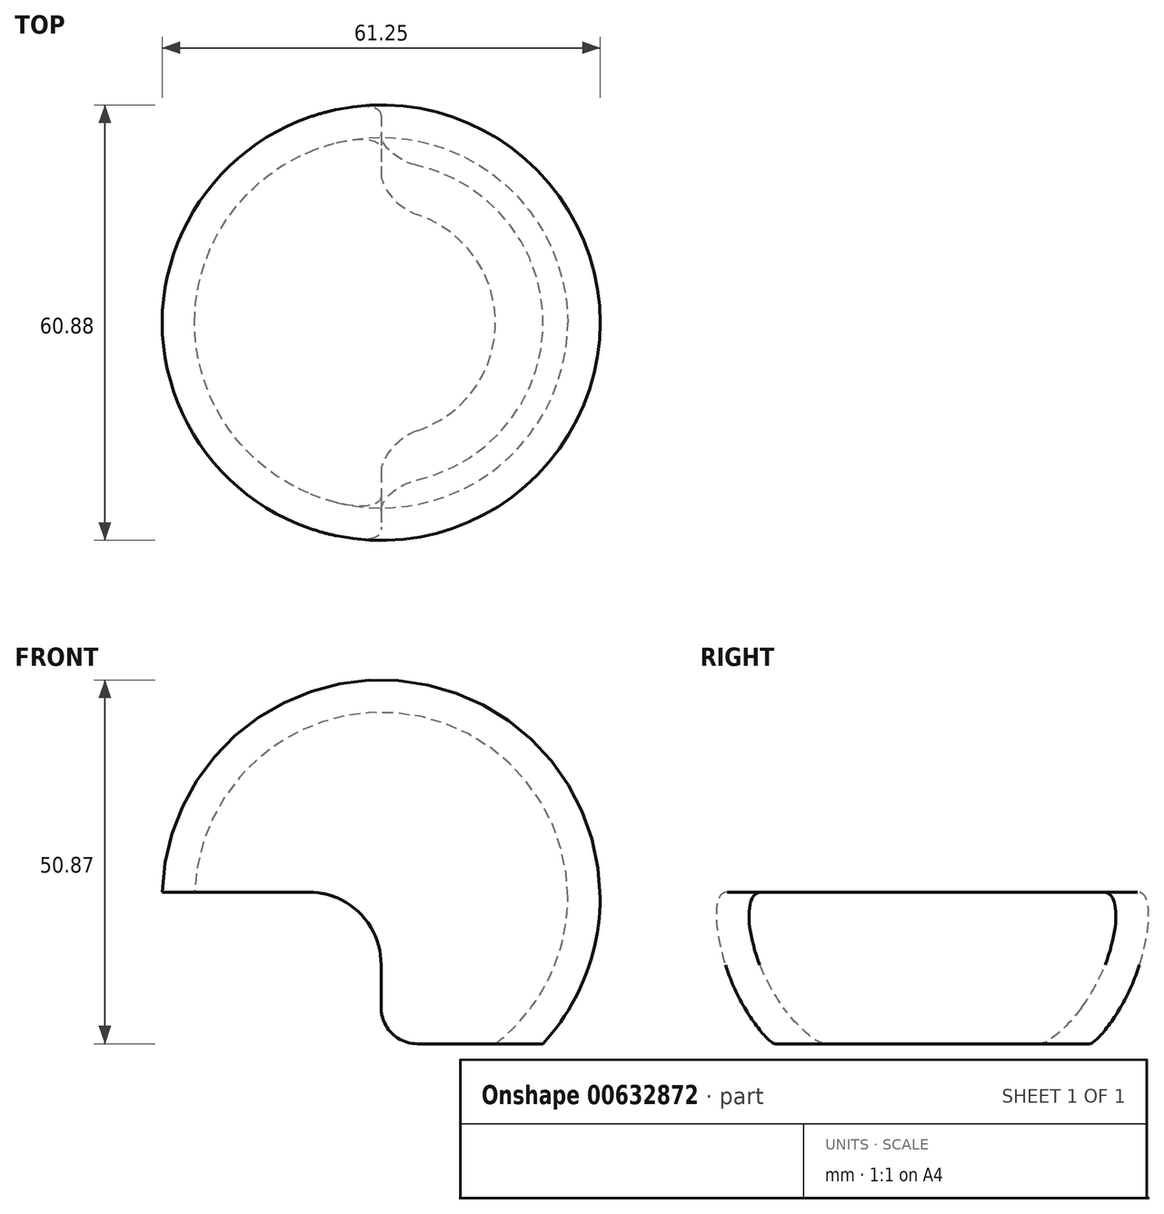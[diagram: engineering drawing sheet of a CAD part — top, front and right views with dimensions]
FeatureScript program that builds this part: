
annotation { "Feature Type Name" : "Feature", "Feature Type Description" : "" }
export const myFeature = defineFeature(function(context is Context, id is Id, definition is map)
    precondition{}
    {
        {
            var Q0;
            Q0=qCreatedBy(makeId("Front.planeOp"),FACE);
            var sketch = newSketch(context, id + "F0", { "sketchPlane" : qUnion([Q0])});
            skArc(sketch, "E0", {"start": v(30.63, 0.2) * mm, "mid": v(0, 30.63) * mm, "end": v(-30.63, 0.2) * mm});
            skLineSegment(sketch, "E1", {"start": v(30.63, 0.2) * mm, "end": v(26.1, 0.2) * mm});
            skArc(sketch, "E2", {"start": v(26.1, 0.2) * mm, "mid": v(0, 26.1) * mm, "end": v(-26.1, 0.2) * mm});
            skLineSegment(sketch, "E3.trimOffspring", {"start": v(-26.1, 0.2) * mm, "end": v(-30.63, 0.2) * mm});
            skSolve(sketch);
        }
        {
            var Q0;
            Q0 = qSketchRegion(id + "F0", true);
            var Q1;
            Q1=sQuery(id+"F0.wireOp",EDGE,"E1");
            revolve(context, id + "F1", {"entities" : qUnion([Q0]), "axis" : qUnion([Q1]), "revolveType" : RevolveType.FULL});
        }
        {
            var Q0;
            Q0=qCreatedBy(makeId("Front.planeOp"),FACE);
            var sketch = newSketch(context, id + "F2", { "sketchPlane" : qUnion([Q0])});
            skLineSegment(sketch, "E4.bottom", {"start": v(0, 0.97) * mm, "end": v(-34.52, 0.97) * mm});
            skLineSegment(sketch, "E4.top", {"start": v(0, -36.46) * mm, "end": v(-34.52, -36.46) * mm});
            skLineSegment(sketch, "E4.left", {"start": v(0, 0.97) * mm, "end": v(0, -36.46) * mm});
            skLineSegment(sketch, "E4.right", {"start": v(-34.52, 0.97) * mm, "end": v(-34.52, -36.46) * mm});
            skLineSegment(sketch, "E5.bottom", {"start": v(0, -36.46) * mm, "end": v(31.12, -36.46) * mm});
            skLineSegment(sketch, "E5.top", {"start": v(0, -20.24) * mm, "end": v(31.12, -20.24) * mm});
            skLineSegment(sketch, "E5.right", {"start": v(31.12, -36.46) * mm, "end": v(31.12, -20.24) * mm});
            skSolve(sketch);
        }
        {
            var Q0;
            Q0 = qSketchRegion(id + "F2", true);
            extrude(context, id + "F3", {"entities" : qUnion([Q0]), "operationType" : NewBodyOperationType.REMOVE, "endBound" : BoundingType.SYMMETRIC, "oppositeDirection" : true, "depth" : 137.16 * mm, "offsetDistance" : 25.4 * mm});
        }
        {
            var Q0;
            Q0=makeQuery(id+"F3.boolean.opBoolean","COPY",EDGE,{"disambiguationData":[OD(1.0)],"derivedFrom":makeQuery(id+"F3.opExtrude","SWEPT_EDGE",EDGE,{"disambiguationData":[OSD([sQuery(id+"F2.wireOp",EDGE,"E4.left"),sQuery(id+"F2.wireOp",EDGE,"E5.top")])]})});
            var Q1;
            Q1=makeQuery(id+"F3.boolean.opBoolean","COPY",EDGE,{"disambiguationData":[OD(0.0)],"derivedFrom":makeQuery(id+"F3.opExtrude","SWEPT_EDGE",EDGE,{"disambiguationData":[OSD([sQuery(id+"F2.wireOp",EDGE,"E4.left"),sQuery(id+"F2.wireOp",EDGE,"E5.top")])]})});
            fillet(context, id + "F4", {"entities" : qUnion([Q0, Q1]), "radius" : 5.08 * mm, "tangentPropagation" : true, "allowEdgeOverflow" : false});
        }
        {
            var Q0;
            Q0=makeQuery(id+"F3.boolean.opBoolean","COPY",EDGE,{"disambiguationData":[OD(1.0)],"derivedFrom":makeQuery(id+"F3.opExtrude","SWEPT_EDGE",EDGE,{"disambiguationData":[OSD([sQuery(id+"F2.wireOp",EDGE,"E4.bottom"),sQuery(id+"F2.wireOp",EDGE,"E4.left")])]})});
            var Q1;
            Q1=makeQuery(id+"F3.boolean.opBoolean","COPY",EDGE,{"disambiguationData":[OD(0.0)],"derivedFrom":makeQuery(id+"F3.opExtrude","SWEPT_EDGE",EDGE,{"disambiguationData":[OSD([sQuery(id+"F2.wireOp",EDGE,"E4.bottom"),sQuery(id+"F2.wireOp",EDGE,"E4.left")])]})});
            fillet(context, id + "F5", {"entities" : qUnion([Q0, Q1]), "radius" : 10.16 * mm, "tangentPropagation" : true, "allowEdgeOverflow" : false});
        }
    });
